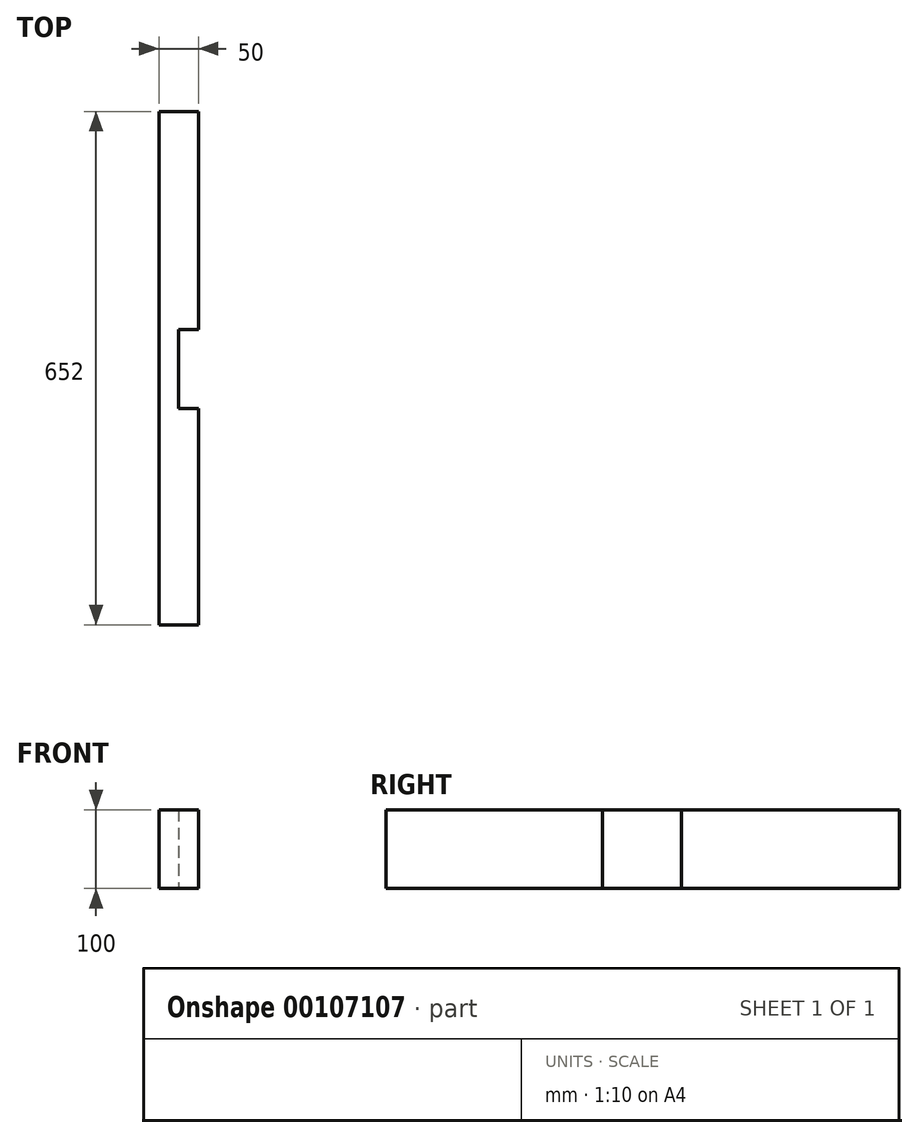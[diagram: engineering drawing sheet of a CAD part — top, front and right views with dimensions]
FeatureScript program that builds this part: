
annotation { "Feature Type Name" : "Feature", "Feature Type Description" : "" }
export const myFeature = defineFeature(function(context is Context, id is Id, definition is map)
    precondition{}
    {
        {
            var Q0;
            Q0=qCreatedBy(makeId("Front.planeOp"),FACE);
            var sketch = newSketch(context, id + "F1", { "sketchPlane" : qUnion([Q0])});
            skLineSegment(sketch, "E0.bottom", {"start": v(0, 0) * mm, "end": v(50, 0) * mm});
            skLineSegment(sketch, "E0.top", {"start": v(0, 100) * mm, "end": v(50, 100) * mm});
            skLineSegment(sketch, "E0.left", {"start": v(0, 0) * mm, "end": v(0, 100) * mm});
            skLineSegment(sketch, "E0.right", {"start": v(50, 0) * mm, "end": v(50, 100) * mm});
            skSolve(sketch);
        }
        {
            var Q0;
            Q0=qSketchRegion(id+"F1",true);
            extrude(context, id + "F2", {"entities" : qUnion([Q0]), "depth" : 652 * mm});
        }
        {
            var Q0;
            Q0=makeQuery(id+"F2.opExtrude","SWEPT_FACE",FACE,{"disambiguationData":[OSD([sQuery(id+"F1.wireOp",EDGE,"E0.right")])]});
            var sketch = newSketch(context, id + "F0", { "sketchPlane" : qUnion([Q0])});
            skLineSegment(sketch, "E1.bottom", {"start": v(-377, 100) * mm, "end": v(-277, 100) * mm});
            skLineSegment(sketch, "E1.top", {"start": v(-377, 0) * mm, "end": v(-277, 0) * mm});
            skLineSegment(sketch, "E1.left", {"start": v(-377, 100) * mm, "end": v(-377, 0) * mm});
            skLineSegment(sketch, "E1.right", {"start": v(-277, 100) * mm, "end": v(-277, 0) * mm});
            skSolve(sketch);
        }
        {
            var Q0;
            Q0=makeQuery(id+"F0.imprint","IMPRINT",FACE,{"disambiguationData":[TD([[makeQuery(id+"F0.imprint","IMPRINT",EDGE,{"derivedFrom":sQuery(id+"F0.wireOp",EDGE,"E1.bottom")}),-1.0]])]});
            extrude(context, id + "F3", {"entities" : qUnion([Q0]), "operationType" : NewBodyOperationType.REMOVE, "oppositeDirection" : true, "depth" : 25 * mm});
        }
    });
